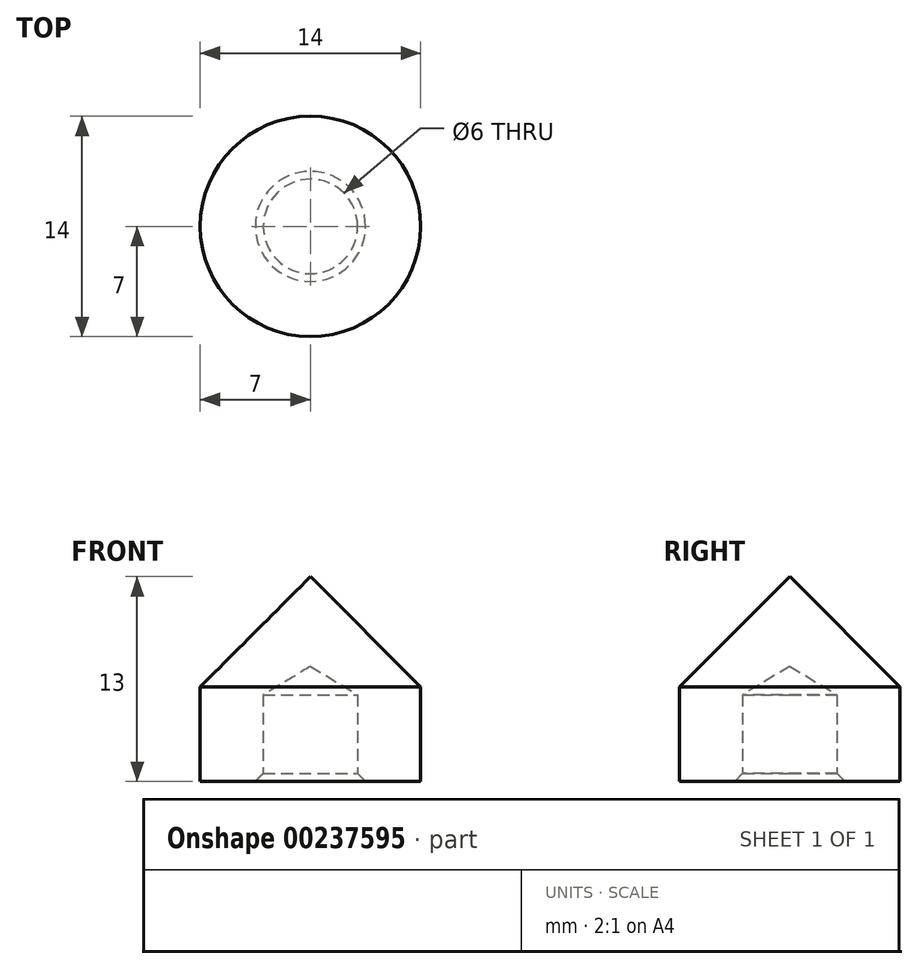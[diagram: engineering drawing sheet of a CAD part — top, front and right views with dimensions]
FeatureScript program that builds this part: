
annotation { "Feature Type Name" : "Feature", "Feature Type Description" : "" }
export const myFeature = defineFeature(function(context is Context, id is Id, definition is map)
    precondition{}
    {
        {
            var Q0;
            Q0=qCreatedBy(makeId("Front.planeOp"),FACE);
            var sketch = newSketch(context, id + "F0", { "sketchPlane" : qUnion([Q0])});
            skLineSegment(sketch, "E0", {"start": v(0, 13) * mm, "end": v(7, 6) * mm});
            skLineSegment(sketch, "E1", {"start": v(7, 6) * mm, "end": v(7, 0) * mm});
            skLineSegment(sketch, "E2", {"start": v(7, 0) * mm, "end": v(0, 0) * mm});
            skLineSegment(sketch, "E3", {"start": v(0, 0) * mm, "end": v(0, 13) * mm});
            skLineSegment(sketch, "E4", {"start": v(0, 16.08) * mm, "end": v(0, -4.73) * mm, "construction": true});
            skSolve(sketch);
        }
        {
            var Q0;
            Q0=makeQuery(id+"F0.imprint","IMPRINT",FACE,{"disambiguationData":[TD([[makeQuery(id+"F0.imprint","IMPRINT",EDGE,{"derivedFrom":sQuery(id+"F0.wireOp",EDGE,"E0")}),-1.0]])]});
            var Q1;
            Q1=sQuery(id+"F0.wireOp",EDGE,"E4");
            revolve(context, id + "F1", {"entities" : qUnion([Q0]), "axis" : qUnion([Q1]), "revolveType" : RevolveType.FULL});
        }
        {
            var Q0;
            Q0=makeQuery(id+"F1.opRevolve","SWEPT_FACE",FACE,{"disambiguationData":[OSD([sQuery(id+"F0.wireOp",EDGE,"E2")])]});
            var sketch = newSketch(context, id + "F2", { "sketchPlane" : qUnion([Q0])});
            skPoint(sketch, "E5", {"position": v(0, 0) * mm});
            skSolve(sketch);
        }
        {
            var Q0;
            Q0=sQuery(id+"F2.wireOp",VERTEX,"E5");
            var Q1;
            Q1=makeQuery(id+"F1.opRevolve","SWEPT_BODY",BODY,{"disambiguationData":[OSD([sQuery(id+"F0.wireOp",EDGE,"E0"),sQuery(id+"F0.wireOp",EDGE,"E1"),sQuery(id+"F0.wireOp",EDGE,"E2"),sQuery(id+"F0.wireOp",EDGE,"E3")])]});
            hole(context, id + "F3", {"style" : HoleStyle.C_SINK, "endStyle" : HoleEndStyle.BLIND, "holeDiameter" : 6 * mm, "cSinkDiameter" : 7 * mm, "cSinkAngle" : 90 * degree, "holeDepth" : 5.5 * mm, "locations" : qUnion([Q0]), "scope" : qUnion([Q1])});
        }
    });
